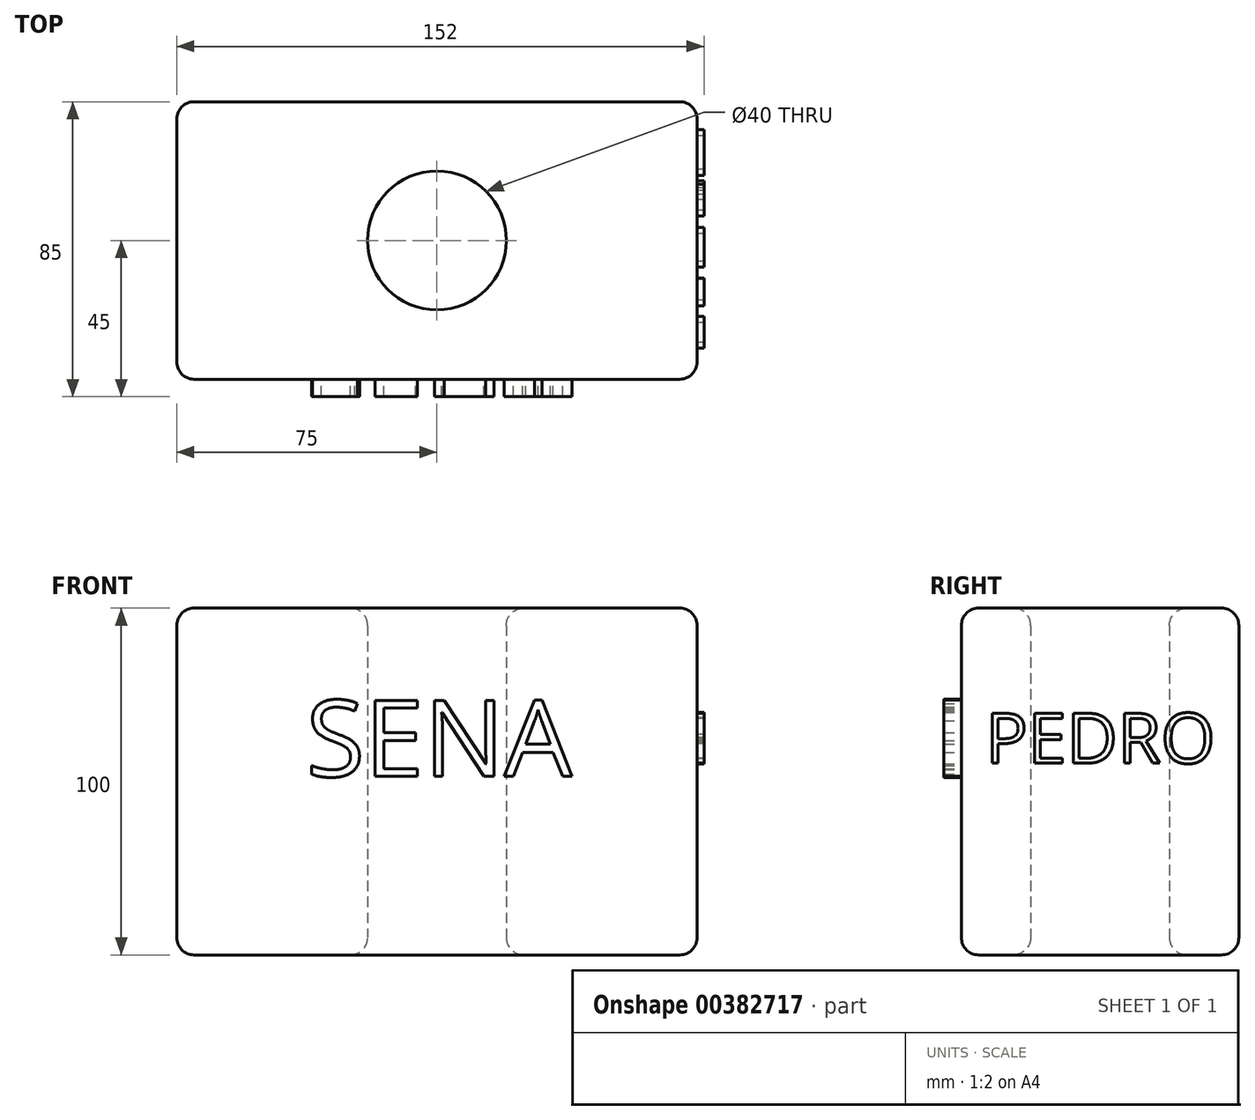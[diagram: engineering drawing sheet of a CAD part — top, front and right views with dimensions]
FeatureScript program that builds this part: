
annotation { "Feature Type Name" : "Feature", "Feature Type Description" : "" }
export const myFeature = defineFeature(function(context is Context, id is Id, definition is map)
    precondition{}
    {
        {
            var Q0;
            Q0=qCreatedBy(makeId("Front.planeOp"),FACE);
            var sketch = newSketch(context, id + "F0", { "sketchPlane" : qUnion([Q0])});
            skLineSegment(sketch, "E0.bottom", {"start": v(75, 50) * mm, "end": v(-75, 50) * mm});
            skLineSegment(sketch, "E0.top", {"start": v(75, -50) * mm, "end": v(-75, -50) * mm});
            skLineSegment(sketch, "E0.left", {"start": v(75, 50) * mm, "end": v(75, -50) * mm});
            skLineSegment(sketch, "E0.right", {"start": v(-75, 50) * mm, "end": v(-75, -50) * mm});
            skPoint(sketch, "E0.middle", {"position": v(0, 0) * mm});
            skSolve(sketch);
        }
        {
            var Q0;
            Q0 = qSketchRegion(id + "F0", true);
            extrude(context, id + "F1", {"entities" : qUnion([Q0]), "endBound" : BoundingType.SYMMETRIC, "depth" : 80 * mm});
        }
        {
            var Q0;
            Q0=qCreatedBy(makeId("Top.planeOp"),FACE);
            var sketch = newSketch(context, id + "F2", { "sketchPlane" : qUnion([Q0])});
            skCircle(sketch, "E1", {"center": v(0, 0) * mm, "radius": 20 * mm});
            skSolve(sketch);
        }
        {
            var Q0;
            Q0 = qSketchRegion(id + "F2", true);
            extrude(context, id + "F3", {"entities" : qUnion([Q0]), "operationType" : NewBodyOperationType.REMOVE, "endBound" : BoundingType.SYMMETRIC, "depth" : 148 * mm});
        }
        {
            var Q0;
            Q0=makeQuery(id+"F1.opExtrude","SWEPT_FACE",FACE,{"disambiguationData":[OSD([sQuery(id+"F0.wireOp",EDGE,"E0.bottom")])]});
            fillet(context, id + "F4", {"entities" : qUnion([Q0]), "radius" : 5 * mm, "tangentPropagation" : true, "allowEdgeOverflow" : false});
        }
        {
            var Q0;
            Q0=makeQuery(id+"F1.opExtrude","CAP_FACE",FACE,{"disambiguationData":[OSD([sQuery(id+"F0.wireOp",EDGE,"E0.bottom"),sQuery(id+"F0.wireOp",EDGE,"E0.top"),sQuery(id+"F0.wireOp",EDGE,"E0.left"),sQuery(id+"F0.wireOp",EDGE,"E0.right")])],"isStart":false});
            var Q1;
            Q1=makeQuery(id+"F1.opExtrude","SWEPT_FACE",FACE,{"disambiguationData":[OSD([sQuery(id+"F0.wireOp",EDGE,"E0.right")])]});
            var Q2;
            Q2=makeQuery(id+"F1.opExtrude","CAP_FACE",FACE,{"disambiguationData":[OSD([sQuery(id+"F0.wireOp",EDGE,"E0.bottom"),sQuery(id+"F0.wireOp",EDGE,"E0.top"),sQuery(id+"F0.wireOp",EDGE,"E0.left"),sQuery(id+"F0.wireOp",EDGE,"E0.right")])],"isStart":true});
            var Q3;
            Q3=makeQuery(id+"F1.opExtrude","SWEPT_FACE",FACE,{"disambiguationData":[OSD([sQuery(id+"F0.wireOp",EDGE,"E0.top")])]});
            fillet(context, id + "F5", {"entities" : qUnion([Q0, Q1, Q2, Q3]), "radius" : 5 * mm, "tangentPropagation" : true, "allowEdgeOverflow" : false});
        }
        {
            var Q0;
            Q0=makeQuery(id+"F1.opExtrude","CAP_FACE",FACE,{"disambiguationData":[OSD([sQuery(id+"F0.wireOp",EDGE,"E0.bottom"),sQuery(id+"F0.wireOp",EDGE,"E0.top"),sQuery(id+"F0.wireOp",EDGE,"E0.left"),sQuery(id+"F0.wireOp",EDGE,"E0.right")])],"isStart":false});
            var sketch = newSketch(context, id + "F6", { "sketchPlane" : qUnion([Q0])});
            skText(sketch, "E2", { "text": "SENA\n", "fontName": "OpenSans-Regular.ttf"});
            const initialGuessF6  = {"E2": [-0.03774, 0.00145, 1, 0, 0.02214]};
            skSetInitialGuess(sketch, initialGuessF6);
            skSolve(sketch);
        }
        {
            var Q0;
            Q0 = qSketchRegion(id + "F6", true);
            extrude(context, id + "F7", {"entities" : qUnion([Q0]), "operationType" : NewBodyOperationType.ADD, "depth" : 5 * mm});
        }
        {
            var Q0;
            Q0=makeQuery(id+"F1.opExtrude","SWEPT_FACE",FACE,{"disambiguationData":[OSD([sQuery(id+"F0.wireOp",EDGE,"E0.left")])]});
            var sketch = newSketch(context, id + "F8", { "sketchPlane" : qUnion([Q0])});
            skText(sketch, "E3", { "text": "PEDRO", "fontName": "OpenSans-Regular.ttf"});
            const initialGuessF8  = {"E3": [-0.03302, 0.00526, 1, 0, 0.01452]};
            skSetInitialGuess(sketch, initialGuessF8);
            skSolve(sketch);
        }
        {
            var Q0;
            Q0 = qSketchRegion(id + "F8", true);
            extrude(context, id + "F9", {"entities" : qUnion([Q0]), "operationType" : NewBodyOperationType.ADD, "depth" : 2 * mm});
        }
    });
